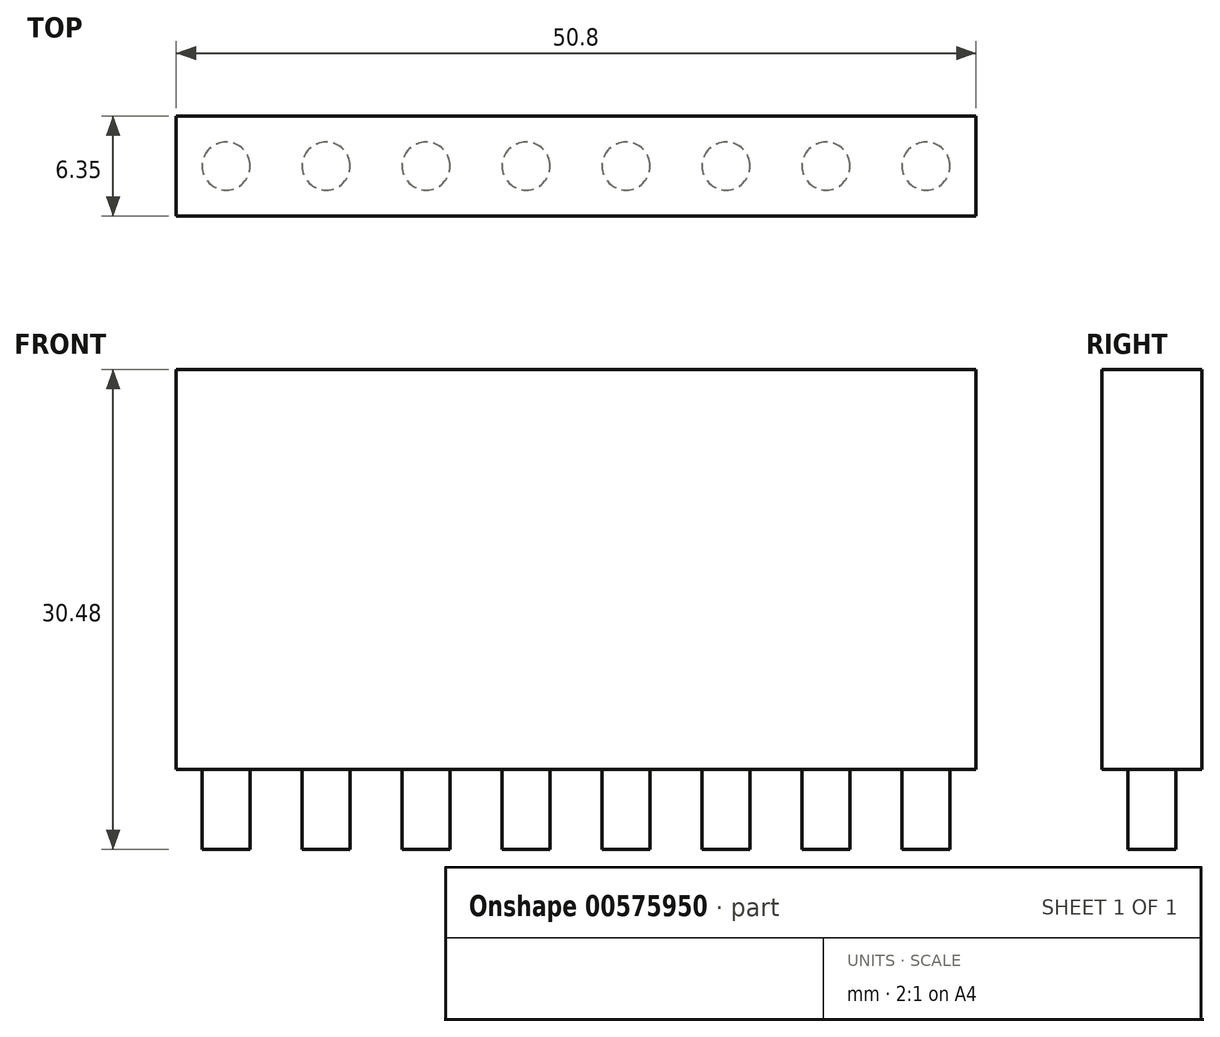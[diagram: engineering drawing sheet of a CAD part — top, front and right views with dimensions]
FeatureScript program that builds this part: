
annotation { "Feature Type Name" : "Feature", "Feature Type Description" : "" }
export const myFeature = defineFeature(function(context is Context, id is Id, definition is map)
    precondition{}
    {
        {
            var Q0;
            Q0=qCreatedBy(makeId("Front.planeOp"),FACE);
            var sketch = newSketch(context, id + "F0", { "sketchPlane" : qUnion([Q0])});
            skLineSegment(sketch, "E0.bottom", {"start": v(25.4, -12.7) * mm, "end": v(-25.4, -12.7) * mm});
            skLineSegment(sketch, "E0.top", {"start": v(25.4, 12.7) * mm, "end": v(-25.4, 12.7) * mm});
            skLineSegment(sketch, "E0.left", {"start": v(25.4, -12.7) * mm, "end": v(25.4, 12.7) * mm});
            skLineSegment(sketch, "E0.right", {"start": v(-25.4, -12.7) * mm, "end": v(-25.4, 12.7) * mm});
            skPoint(sketch, "E0.middle", {"position": v(0, 0) * mm});
            skSolve(sketch);
        }
        {
            var Q0;
            Q0 = qSketchRegion(id + "F0", true);
            extrude(context, id + "F1", {"entities" : qUnion([Q0]), "depth" : 6.35 * mm, "offsetDistance" : 25.4 * mm});
        }
        {
            var Q0;
            Q0=makeQuery(id+"F1.opExtrude","SWEPT_FACE",FACE,{"disambiguationData":[OSD([sQuery(id+"F0.wireOp",EDGE,"E0.bottom")])]});
            var sketch = newSketch(context, id + "F2", { "sketchPlane" : qUnion([Q0])});
            skLineSegment(sketch, "E1", {"start": v(-25.4, 3.18) * mm, "end": v(-22.23, 3.18) * mm});
            skPoint(sketch, "E1.endSnap0", {"position": v(-25.4, 3.18) * mm});
            skCircle(sketch, "E2", {"center": v(-22.23, 3.18) * mm, "radius": 1.52 * mm});
            skCircle(sketch, "E3.1.0.0", {"center": v(-15.88, 3.18) * mm, "radius": 1.52 * mm});
            skCircle(sketch, "E3.2.0.0", {"center": v(-9.53, 3.18) * mm, "radius": 1.52 * mm});
            skCircle(sketch, "E3.3.0.0", {"center": v(-3.18, 3.18) * mm, "radius": 1.52 * mm});
            skCircle(sketch, "E3.4.0.0", {"center": v(3.18, 3.18) * mm, "radius": 1.52 * mm});
            skCircle(sketch, "E3.5.0.0", {"center": v(9.53, 3.18) * mm, "radius": 1.52 * mm});
            skCircle(sketch, "E3.6.0.0", {"center": v(15.88, 3.18) * mm, "radius": 1.52 * mm});
            skCircle(sketch, "E3.7.0.0", {"center": v(22.23, 3.18) * mm, "radius": 1.52 * mm});
            skLineSegment(sketch, "E3.direction1", {"start": v(-22.23, 3.18) * mm, "end": v(-15.88, 3.18) * mm, "construction": true});
            skSolve(sketch);
        }
        {
            var Q0;
            Q0 = qSketchRegion(id + "F2", true);
            extrude(context, id + "F3", {"entities" : qUnion([Q0]), "operationType" : NewBodyOperationType.ADD, "depth" : 5.08 * mm, "offsetDistance" : 25.4 * mm});
        }
    });
